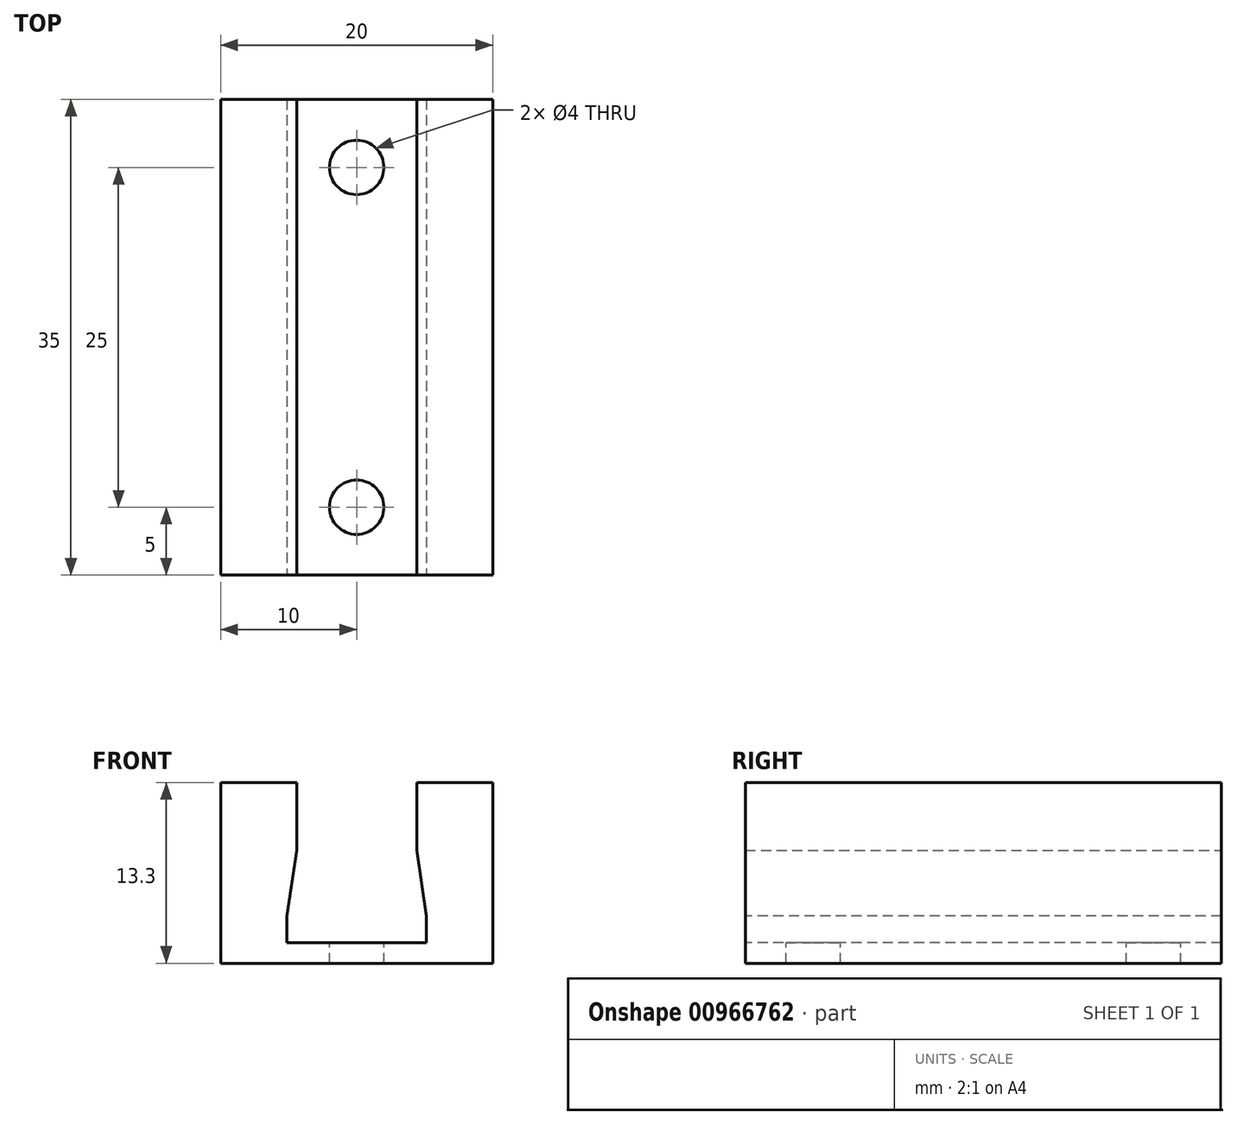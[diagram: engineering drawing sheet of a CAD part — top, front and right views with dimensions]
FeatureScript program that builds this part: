
annotation { "Feature Type Name" : "Feature", "Feature Type Description" : "" }
export const myFeature = defineFeature(function(context is Context, id is Id, definition is map)
    precondition{}
    {
        {
            var Q0;
            Q0=qCreatedBy(makeId("Front.planeOp"),FACE);
            var sketch = newSketch(context, id + "F0", { "sketchPlane" : qUnion([Q0])});
            skLineSegment(sketch, "E0.bottom", {"start": v(4.15, -2.65) * mm, "end": v(-4.15, -2.65) * mm});
            skLineSegment(sketch, "E0.top", {"start": v(4.15, 2.65) * mm, "end": v(-4.15, 2.65) * mm});
            skLineSegment(sketch, "E0.left", {"start": v(5.15, -1.65) * mm, "end": v(5.15, 1.65) * mm});
            skLineSegment(sketch, "E0.right", {"start": v(-5.15, -1.65) * mm, "end": v(-5.15, 1.65) * mm});
            skPoint(sketch, "E0.middle", {"position": v(0, 0) * mm});
            skPoint(sketch, "E1.visualSharp", {"position": v(-5.15, 2.65) * mm});
            skArc(sketch, "E1.filletArc", {"start": v(-4.15, 2.65) * mm, "mid": v(-4.86, 2.36) * mm, "end": v(-5.15, 1.65) * mm});
            skPoint(sketch, "E2.visualSharp", {"position": v(5.15, 2.65) * mm});
            skArc(sketch, "E2.filletArc", {"start": v(5.15, 1.65) * mm, "mid": v(4.86, 2.36) * mm, "end": v(4.15, 2.65) * mm});
            skPoint(sketch, "E3.visualSharp", {"position": v(5.15, -2.65) * mm});
            skArc(sketch, "E3.filletArc", {"start": v(4.15, -2.65) * mm, "mid": v(4.86, -2.36) * mm, "end": v(5.15, -1.65) * mm});
            skPoint(sketch, "E4.visualSharp", {"position": v(-5.15, -2.65) * mm});
            skArc(sketch, "E4.filletArc", {"start": v(-5.15, -1.65) * mm, "mid": v(-4.86, -2.36) * mm, "end": v(-4.15, -2.65) * mm});
            skLineSegment(sketch, "E5.2", {"start": v(4.15, 4.15) * mm, "end": v(-4.15, 4.15) * mm});
            skLineSegment(sketch, "E5.7", {"start": v(4.15, -4.15) * mm, "end": v(-4.15, -4.15) * mm});
            skPoint(sketch, "E6.visualSharp", {"position": v(-8.7, 0) * mm});
            skPoint(sketch, "E7.visualSharp", {"position": v(8.7, 0) * mm});
            skLineSegment(sketch, "E8", {"start": v(-4.15, -4.15) * mm, "end": v(-10, -4.15) * mm});
            skLineSegment(sketch, "E9", {"start": v(4.15, -4.15) * mm, "end": v(10, -4.15) * mm});
            skLineSegment(sketch, "E10", {"start": v(4.15, 4.15) * mm, "end": v(10, 4.15) * mm});
            skLineSegment(sketch, "E11", {"start": v(10, 4.15) * mm, "end": v(10, -4.15) * mm});
            skLineSegment(sketch, "E12", {"start": v(-4.15, 4.15) * mm, "end": v(-10, 4.15) * mm});
            skLineSegment(sketch, "E13", {"start": v(-10, 4.15) * mm, "end": v(-10, -4.15) * mm});
            skSolve(sketch);
        }
        {
            var Q0;
            Q0=makeQuery(id+"F0.imprint","IMPRINT",FACE,{"disambiguationData":[TD([[makeQuery(id+"F0.imprint","IMPRINT",EDGE,{"derivedFrom":sQuery(id+"F0.wireOp",EDGE,"E0.bottom")}),1.0]])]});
            var Q1;
            Q1=makeQuery(id+"F0.imprint","IMPRINT",FACE,{"disambiguationData":[TD([[makeQuery(id+"F0.imprint","IMPRINT",EDGE,{"derivedFrom":sQuery(id+"F0.wireOp",EDGE,"E0.bottom")}),-1.0]])]});
            extrude(context, id + "F1", {"entities" : qUnion([Q0, Q1]), "depth" : 35 * mm, "offsetDistance" : 25 * mm});
        }
        {
            var Q0;
            Q0=makeQuery(id+"F1.opExtrude","SWEPT_FACE",FACE,{"disambiguationData":[OSD([sQuery(id+"F0.wireOp",EDGE,"E5.2")])]});
            var sketch = newSketch(context, id + "F2", { "sketchPlane" : qUnion([Q0])});
            skCircle(sketch, "E14", {"center": v(0, -5) * mm, "radius": 2 * mm});
            skCircle(sketch, "E15", {"center": v(0, -30) * mm, "radius": 2 * mm});
            skSolve(sketch);
        }
        {
            var Q0;
            Q0=makeQuery(id+"F2.imprint","IMPRINT",FACE,{"disambiguationData":[TD([[makeQuery(id+"F2.imprint","IMPRINT",EDGE,{"derivedFrom":sQuery(id+"F2.wireOp",EDGE,"S33YdpTx-NKYe-flyp-kQUo-xBa4HNO2xXOk")}),1.0]])]});
            var Q1;
            Q1=makeQuery(id+"F2.imprint","IMPRINT",FACE,{"disambiguationData":[TD([[makeQuery(id+"F2.imprint","IMPRINT",EDGE,{"derivedFrom":sQuery(id+"F2.wireOp",EDGE,"E14")}),1.0]])]});
            var Q2;
            Q2=makeQuery(id+"F2.imprint","IMPRINT",FACE,{"disambiguationData":[TD([[makeQuery(id+"F2.imprint","IMPRINT",EDGE,{"derivedFrom":sQuery(id+"F2.wireOp",EDGE,"E15")}),1.0]])]});
            extrude(context, id + "F3", {"entities" : qUnion([Q0, Q1, Q2]), "operationType" : NewBodyOperationType.REMOVE, "endBound" : BoundingType.THROUGH_ALL, "oppositeDirection" : true, "depth" : 25 * mm, "offsetDistance" : 25 * mm});
        }
        {
            var Q0;
            Q0=qCreatedBy(makeId("Top.planeOp"),FACE);
            cPlane(context, id + "F4", {"entities" : qUnion([Q0]), "cplaneType" : CPlaneType.OFFSET, "offset" : 4.6 * mm, "width" : 150 * mm, "height" : 150 * mm});
        }
        {
            var Q0;
            Q0=qCreatedBy(id+"F4.planeOp",FACE);
            var sketch = newSketch(context, id + "F5", { "sketchPlane" : qUnion([Q0])});
            skLineSegment(sketch, "E16.bottom", {"start": v(8, 3.7) * mm, "end": v(-8, 3.7) * mm});
            skLineSegment(sketch, "E16.left", {"start": v(8, 3.7) * mm, "end": v(8, -3.7) * mm});
            skLineSegment(sketch, "E16.right", {"start": v(-8, 3.7) * mm, "end": v(-8, -3.7) * mm});
            skPoint(sketch, "E16.middle", {"position": v(0, 0) * mm});
            skArc(sketch, "E17", {"start": v(8, -3.7) * mm, "mid": v(0, -0.15) * mm, "end": v(-8, -3.7) * mm});
            skSolve(sketch);
        }
        {
            var Q0;
            Q0=makeQuery(id+"F1.opExtrude","CAP_FACE",FACE,{"disambiguationData":[OSD([sQuery(id+"F0.wireOp",EDGE,"E0.bottom"),sQuery(id+"F0.wireOp",EDGE,"E0.top"),sQuery(id+"F0.wireOp",EDGE,"E0.left"),sQuery(id+"F0.wireOp",EDGE,"E0.right"),sQuery(id+"F0.wireOp",EDGE,"E1.filletArc"),sQuery(id+"F0.wireOp",EDGE,"E2.filletArc"),sQuery(id+"F0.wireOp",EDGE,"E3.filletArc"),sQuery(id+"F0.wireOp",EDGE,"E4.filletArc"),sQuery(id+"F0.wireOp",EDGE,"E5.0"),sQuery(id+"F0.wireOp",EDGE,"E5.2"),sQuery(id+"F0.wireOp",EDGE,"E5.3"),sQuery(id+"F0.wireOp",EDGE,"E5.4"),sQuery(id+"F0.wireOp",EDGE,"E5.6"),sQuery(id+"F0.wireOp",EDGE,"E5.7"),sQuery(id+"F0.wireOp",EDGE,"j0FmOnv8-2giZ-Heyp-FxGT-kFQuoCsbufpf"),sQuery(id+"F0.wireOp",EDGE,"e1dd9d24-0ac2-42c2-a643-89ccc1da2aac0.MirrorCS"),sQuery(id+"F0.wireOp",EDGE,"ffd52f68-4b42-4839-91c0-644cf02551480.MirrorCS"),sQuery(id+"F0.wireOp",EDGE,"f7e891a1-da83-4fae-8f2e-2a1de3fda1f90.MirrorCS"),sQuery(id+"F0.wireOp",EDGE,"E6.filletArc"),sQuery(id+"F0.wireOp",EDGE,"E7.filletArc")])],"isStart":false});
            cPlane(context, id + "F6", {"entities" : qUnion([Q0]), "cplaneType" : CPlaneType.OFFSET, "offset" : 0 * mm, "width" : 150 * mm, "height" : 150 * mm});
        }
        {
            var Q0;
            Q0=qCreatedBy(id+"F6.planeOp",FACE);
            var sketch = newSketch(context, id + "F7", { "sketchPlane" : qUnion([Q0])});
            skLineSegment(sketch, "E18", {"start": v(0, -2.65) * mm, "end": v(5.13, -2.65) * mm});
            skLineSegment(sketch, "E19", {"start": v(5.13, -2.65) * mm, "end": v(5.13, -0.66) * mm});
            skLineSegment(sketch, "E20", {"start": v(5.13, -0.66) * mm, "end": v(4.39, 4.35) * mm});
            skLineSegment(sketch, "E21", {"start": v(4.39, 4.35) * mm, "end": v(0, 4.35) * mm});
            skLineSegment(sketch, "E22.MirrorCS", {"start": v(-4.39, 4.35) * mm, "end": v(0, 4.35) * mm});
            skLineSegment(sketch, "E23.MirrorCS", {"start": v(-5.13, -0.66) * mm, "end": v(-4.39, 4.35) * mm});
            skLineSegment(sketch, "E24.MirrorCS", {"start": v(-5.13, -2.65) * mm, "end": v(-5.13, -0.66) * mm});
            skLineSegment(sketch, "E25.MirrorCS", {"start": v(0, -2.65) * mm, "end": v(-5.13, -2.65) * mm});
            skSolve(sketch);
        }
        {
            var Q0;
            Q0=makeQuery(id+"F7.imprint","IMPRINT",FACE,{"disambiguationData":[TD([[makeQuery(id+"F7.imprint","IMPRINT",EDGE,{"derivedFrom":sQuery(id+"F7.wireOp",EDGE,"E18")}),1.0]])]});
            extrude(context, id + "F8", {"entities" : qUnion([Q0]), "operationType" : NewBodyOperationType.REMOVE, "endBound" : BoundingType.THROUGH_ALL, "oppositeDirection" : true, "depth" : 150 * mm, "offsetDistance" : 25 * mm});
        }
        {
            var Q0;
            {var subQ0=sQuery(id+"F0.wireOp",EDGE,"E13");var subQ1=sQuery(id+"F0.wireOp",EDGE,"E12");var subQ3=sQuery(id+"F0.wireOp",EDGE,"E10");var subQ7=sQuery(id+"F0.wireOp",EDGE,"E5.2");Q0=makeQuery(id+"F8.boolean.opBoolean","SPLIT",FACE,{"disambiguationData":[TD([makeQuery(id+"F1.opExtrude","SWEPT_FACE",FACE,{"disambiguationData":[OSD([subQ0])]})])],"derivedFrom":makeQuery(id+"F1.opExtrude","SWEPT_FACE",FACE,{"disambiguationData":[OSD([subQ7,subQ3,subQ1])]})});}
            var Q1;
            {var subQ1=sQuery(id+"F0.wireOp",EDGE,"E12");var subQ2=sQuery(id+"F0.wireOp",EDGE,"E11");var subQ3=sQuery(id+"F0.wireOp",EDGE,"E10");var subQ7=sQuery(id+"F0.wireOp",EDGE,"E5.2");Q1=makeQuery(id+"F8.boolean.opBoolean","SPLIT",FACE,{"disambiguationData":[TD([makeQuery(id+"F1.opExtrude","SWEPT_FACE",FACE,{"disambiguationData":[OSD([subQ2])]})])],"derivedFrom":makeQuery(id+"F1.opExtrude","SWEPT_FACE",FACE,{"disambiguationData":[OSD([subQ7,subQ3,subQ1])]})});}
            extrude(context, id + "F9", {"entities" : qUnion([Q0, Q1]), "operationType" : NewBodyOperationType.ADD, "depth" : 5 * mm, "offsetDistance" : 25 * mm});
        }
    });
